# Revit family: ML-2L3K-1-DB
name_source: partatom
category: Lighting Fixtures
units: mm (PartAtom-declared; Revit-internal decimal feet)

## family parameters
Cut with Voids When Loaded = No
Host = Face
Light Source = No
OmniClass Number = 23.80.70.11.14.17
OmniClass Title = Direct/Indirect
Part Type = Normal
Room Calculation Point = No
Round Connector Dimension = Use Diameter
Shared = Yes

## types (1)
- ML-2L3K-1-DB
    Apparent Load = 27 VA
    Assembly Code = D5020200
    Connector Description = Lighting Connector
    Default Elevation = 48 "
    Description = Marshal LED Twin Head Motion Sensor Kit, Light Source: LED, LED, Light Output: 2,104 lm, Mounting Type: ceiling;wall, 3000 K, 83 CRI, Wattage: 26.6 W, Dark Bronze
    Features = Attractive security floodlight improves safety and replaces bulky
outdated fixtures
• Powerful LED system saves energy and maintenance over traditional
lighting sources
• Includes adjustable settings for time, sensitivity, and distance
• Aimable PIR occupancy sensor has 180° coverage, perfect for outdoor
applications
• CSA listed to UL1598 for use in wet locations
    Fixture distribution = Direct
    Glass = White Glass
    Gold = Gold
    Housing Material = Paint -  Textured Camera Black
    Lamp = LED
    Length = 12.75 "
    Load Classification = Lighting
    Manufacturer = EXO
    Model = ML-2L3K-1-DB
    Power Factor = 1
    URL = https://www.currentlighting.com
    Voltage = 120 V
    Warranty = 5 years Warranty
    Wattage Comments = 27W
    Watts = 27 W

## geometry (parser evidence)
native form markers: Sweep x8
no freeform markers — native parametric forms only
